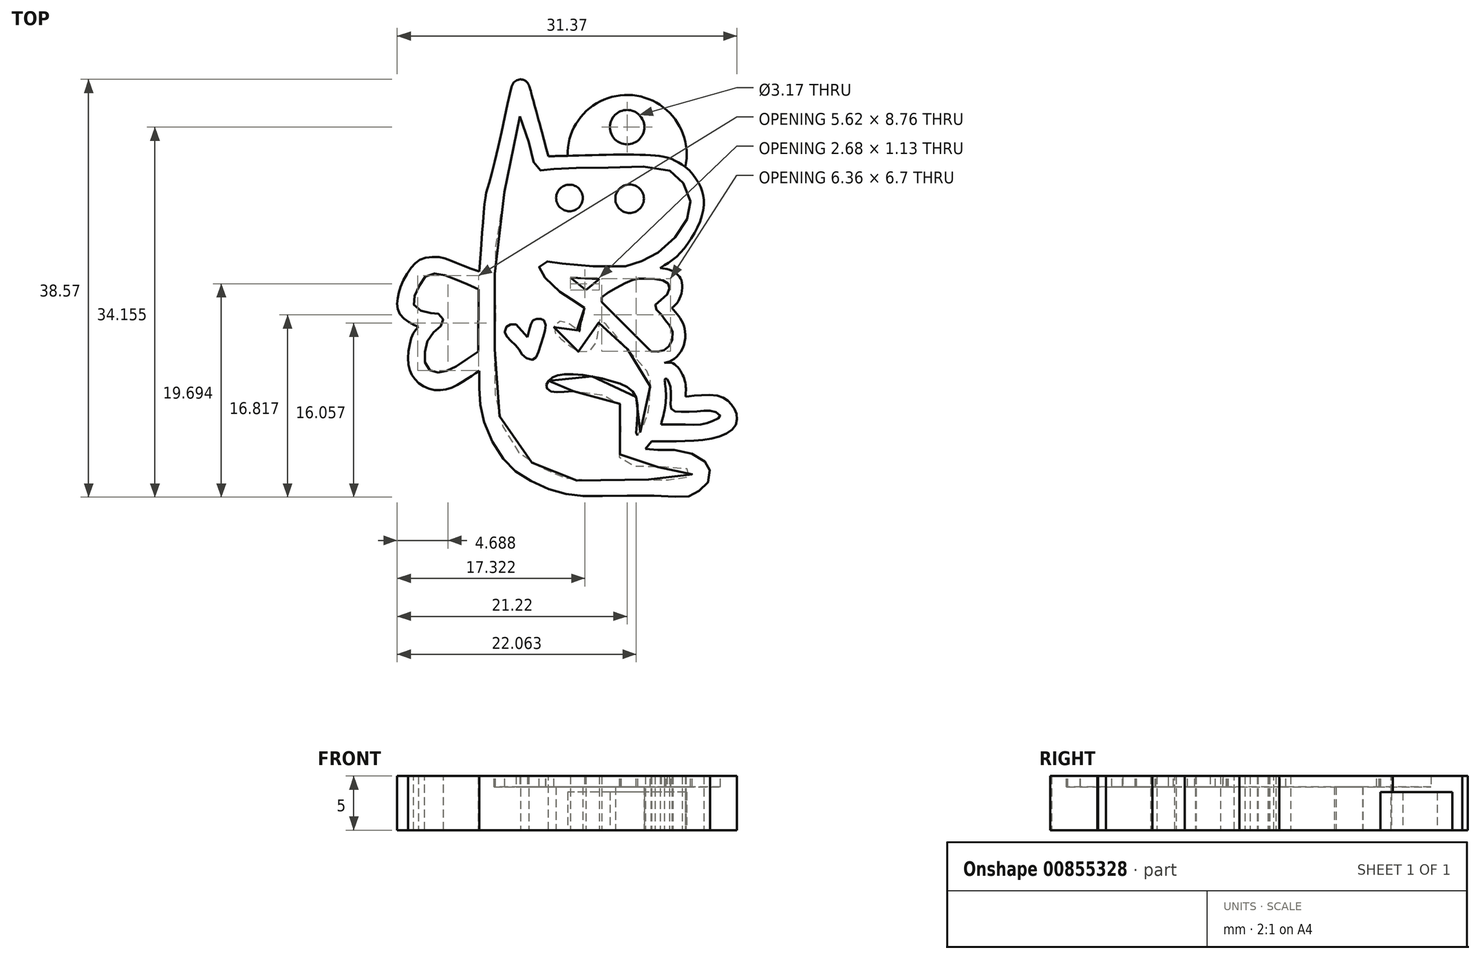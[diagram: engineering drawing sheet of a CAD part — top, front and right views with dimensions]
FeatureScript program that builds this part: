
annotation { "Feature Type Name" : "Feature", "Feature Type Description" : "" }
export const myFeature = defineFeature(function(context is Context, id is Id, definition is map)
    precondition{}
    {
        {
            var Q0;
            Q0=qCreatedBy(makeId("Top.planeOp"),FACE);
            var sketch = newSketch(context, id + "F0", { "sketchPlane" : qUnion([Q0])});
            skFitSpline(sketch, "E0", {"points": [v(-7.48, 15.74) * mm, v(-8.03, 15.56) * mm, v(-8.57, 13.92) * mm, v(-10.3, 6.44) * mm, v(-10.66, 5.2) * mm, v(-10.89, 3.24) * mm, v(-11.2, -1.02) * mm, v(-11.27, -2) * mm], "startDerivative": vector(-8.23, -1.23) * mm, "endDerivative": vector(-0.55, -7.97) * mm});
            skFitSpline(sketch, "E1", {"points": [v(-11.27, -2) * mm, v(-13.6, -1.14) * mm, v(-14.83, -0.68) * mm, v(-16.51, -0.82) * mm, v(-17.49, -1.57) * mm, v(-18.53, -3.31) * mm, v(-18.83, -4.6) * mm, v(-18.76, -5.67) * mm, v(-17.85, -6.63) * mm, v(-16.92, -7.1) * mm], "startDerivative": vector(-17.8, 6.14) * mm, "endDerivative": vector(9.73, -4.22) * mm});
            skFitSpline(sketch, "E2", {"points": [v(-16.92, -7.1) * mm, v(-17.49, -7.96) * mm, v(-17.85, -10.32) * mm, v(-17.3, -11.86) * mm, v(-15.85, -12.84) * mm, v(-14.06, -12.82) * mm, v(-12.36, -11.89) * mm, v(-11.27, -11.18) * mm], "startDerivative": vector(-5.4, -6.2) * mm, "endDerivative": vector(8.14, 5.18) * mm});
            skFitSpline(sketch, "E3", {"points": [v(-11.27, -11.18) * mm, v(-11.27, -13.54) * mm, v(-10.82, -15.97) * mm, v(-9.19, -19.15) * mm, v(-7.44, -20.82) * mm, v(-4.72, -22.14) * mm, v(-2.27, -22.7) * mm, v(0.89, -22.7) * mm, v(6.17, -22.75) * mm, v(8, -22.77) * mm, v(8.96, -22.3) * mm, v(9.87, -21.4) * mm, v(9.98, -20.26) * mm, v(9.57, -19.58) * mm, v(7.76, -18.62) * mm, v(5.35, -18.47) * mm, v(4.06, -18.4) * mm], "startDerivative": vector(-0.97, -36.57) * mm, "endDerivative": vector(-24.45, 2.03) * mm});
            skFitSpline(sketch, "E4", {"points": [v(4.06, -18.4) * mm, v(4.63, -17.67) * mm], "startDerivative": vector(0.57, 0.73) * mm, "endDerivative": vector(0.57, 0.73) * mm});
            skFitSpline(sketch, "E5", {"points": [v(4.63, -17.67) * mm, v(7.4, -17.67) * mm, v(10.52, -17.35) * mm, v(12.3, -16.33) * mm, v(12.45, -15.15) * mm, v(11.89, -14.16) * mm, v(10.77, -13.48) * mm, v(8.46, -13.48) * mm, v(7.76, -13.54) * mm], "startDerivative": vector(17.04, -0.15) * mm, "endDerivative": vector(-7.1, -0.7) * mm});
            skFitSpline(sketch, "E6", {"points": [v(7.76, -13.54) * mm, v(7.76, -12.48) * mm, v(7.42, -11.41) * mm, v(6.6, -10.48) * mm, v(5.78, -10.44) * mm], "startDerivative": vector(0.25, 4.28) * mm, "endDerivative": vector(-3.79, -0.53) * mm});
            skFitSpline(sketch, "E7", {"points": [v(5.78, -10.44) * mm, v(6.77, -10.03) * mm, v(7.64, -8.63) * mm, v(7.62, -7.1) * mm, v(7.13, -6.15) * mm, v(6.5, -5.37) * mm], "startDerivative": vector(5.5, 1.36) * mm, "endDerivative": vector(-3.67, 4.26) * mm});
            skFitSpline(sketch, "E8", {"points": [v(6.5, -5.37) * mm, v(7.15, -4.63) * mm, v(7.45, -3.35) * mm, v(7.2, -2.46) * mm, v(6.37, -1.89) * mm, v(5.41, -1.67) * mm], "startDerivative": vector(3.67, 3.27) * mm, "endDerivative": vector(-4.99, 0.71) * mm});
            skFitSpline(sketch, "E9", {"points": [v(5.41, -1.67) * mm, v(6.75, -0.77) * mm, v(8.14, 0.84) * mm, v(9.27, 3.14) * mm, v(9.4, 4.89) * mm, v(9, 6.06) * mm, v(7.95, 7.48) * mm, v(6.5, 8.37) * mm, v(5.41, 8.65) * mm, v(2.36, 8.8) * mm, v(-2.68, 8.7) * mm, v(-4.9, 8.64) * mm], "startDerivative": vector(17.1, 10.03) * mm, "endDerivative": vector(-20.94, -0.48) * mm});
            skFitSpline(sketch, "E10", {"points": [v(-4.9, 8.64) * mm, v(-6.63, 14.99) * mm, v(-6.71, 15.22) * mm], "startDerivative": vector(-2.7, 10.15) * mm, "endDerivative": vector(-0.37, 0.92) * mm});
            skFitSpline(sketch, "E11", {"points": [v(-6.71, 15.22) * mm, v(-6.9, 15.5) * mm, v(-7.21, 15.7) * mm, v(-7.48, 15.74) * mm], "startDerivative": vector(-0.44, 0.89) * mm, "endDerivative": vector(-0.86, 0.07) * mm});
            skFitSpline(sketch, "E12", {"points": [v(-11.36, -3.64) * mm, v(-12.73, -3.02) * mm, v(-14.07, -2.49) * mm, v(-15.1, -2.2) * mm, v(-16.11, -2.34) * mm, v(-16.74, -3.17) * mm, v(-17.27, -4.33) * mm, v(-17.3, -5.09) * mm, v(-16.72, -5.6) * mm, v(-15.75, -5.84) * mm, v(-15.14, -5.88) * mm, v(-14.73, -6.22) * mm, v(-14.6, -6.6) * mm, v(-14.98, -7.17) * mm, v(-15.66, -7.76) * mm, v(-16.2, -8.8) * mm, v(-16.33, -9.95) * mm, v(-16.13, -10.83) * mm, v(-15.5, -11.28) * mm, v(-14.81, -11.3) * mm, v(-14.02, -11.09) * mm, v(-12.85, -10.4) * mm, v(-11.39, -9.4) * mm], "startDerivative": vector(-23.85, 10.92) * mm, "endDerivative": vector(24.08, 16.28) * mm});
            skFitSpline(sketch, "E13", {"points": [v(-11.39, -9.4) * mm, v(-11.36, -3.64) * mm], "startDerivative": vector(0.02, 5.77) * mm, "endDerivative": vector(0.02, 5.77) * mm});
            skFitSpline(sketch, "E14", {"points": [v(0.02, -4.84) * mm, v(0.02, -4.37) * mm], "startDerivative": vector(0, 0.47) * mm, "endDerivative": vector(0, 0.47) * mm});
            skFitSpline(sketch, "E15", {"points": [v(0.02, -4.37) * mm, v(1, -3.7) * mm, v(2.53, -2.93) * mm, v(3.25, -2.69) * mm, v(4.18, -2.67) * mm, v(5.54, -2.79) * mm, v(6.13, -3.09) * mm, v(6.26, -3.5) * mm, v(5.96, -4.24) * mm, v(5.03, -4.98) * mm, v(4.98, -5.4) * mm, v(5.5, -5.94) * mm, v(6.02, -6.68) * mm, v(6.5, -7.36) * mm, v(6.52, -8.33) * mm, v(6.04, -9.12) * mm, v(5.38, -9.38) * mm, v(4.55, -9.36) * mm], "startDerivative": vector(12.8, 9.65) * mm, "endDerivative": vector(-14.93, 1.2) * mm});
            skFitSpline(sketch, "E16", {"points": [v(4.55, -9.36) * mm, v(0.02, -4.84) * mm], "startDerivative": vector(-4.52, 4.52) * mm, "endDerivative": vector(-4.52, 4.52) * mm});
            skFitSpline(sketch, "E17", {"points": [v(-2.88, -2.57) * mm, v(-1.45, -3.7) * mm], "startDerivative": vector(1.43, -1.13) * mm, "endDerivative": vector(1.43, -1.13) * mm});
            skFitSpline(sketch, "E18", {"points": [v(-1.45, -3.7) * mm, v(-0.2, -2.7) * mm], "startDerivative": vector(1.25, 1) * mm, "endDerivative": vector(1.25, 1) * mm});
            skFitSpline(sketch, "E19", {"points": [v(-0.2, -2.7) * mm, v(-2.88, -2.57) * mm], "startDerivative": vector(-2.68, 0.14) * mm, "endDerivative": vector(-2.68, 0.14) * mm});
            skCircle(sketch, "E20", {"center": v(-2.96, 4.79) * mm, "radius": 1.23 * mm});
            skCircle(sketch, "E21", {"center": v(2.6, 4.72) * mm, "radius": 1.32 * mm});
            skFitSpline(sketch, "E22", {"points": [v(-7.53, 12.33) * mm, v(-8.43, 7.98) * mm, v(-9.84, -0.28) * mm, v(-9.8, -3.59) * mm, v(-9.88, -9.71) * mm, v(-9.75, -13.89) * mm, v(-8.61, -17.38) * mm, v(-6.75, -19.47) * mm, v(-4.53, -20.55) * mm, v(-2.76, -21.23) * mm, v(1.1, -21.23) * mm, v(6.04, -21.23) * mm, v(7.76, -21.1) * mm, v(8.35, -20.74) * mm, v(8.22, -20.5) * mm, v(7.72, -20.15) * mm, v(6.08, -20.06) * mm, v(2.82, -19.96) * mm, v(1.73, -19.51) * mm, v(1.82, -17.97) * mm, v(1.68, -14.8) * mm, v(1.64, -14.11) * mm, v(-0.04, -13.39) * mm, v(-3.03, -13.07) * mm, v(-4.67, -13.07) * mm, v(-5.12, -12.57) * mm, v(-4.8, -12.03) * mm, v(-4.03, -11.57) * mm, v(-1.63, -11.57) * mm, v(1.37, -12.25) * mm, v(3, -13.2) * mm, v(3.32, -15.38) * mm, v(3.27, -17.15) * mm, v(4.13, -15.6) * mm, v(4.45, -13.66) * mm, v(4.5, -12.2) * mm, v(4.31, -11.4) * mm, v(2.5, -9.3) * mm, v(0.55, -7.04) * mm, v(-0.18, -6.45) * mm, v(-0.31, -7.67) * mm, v(-1.08, -9.35) * mm, v(-2.26, -9.35) * mm, v(-3.44, -8.49) * mm, v(-4.21, -7.76) * mm, v(-4.35, -7) * mm, v(-3.85, -6.58) * mm, v(-2.94, -6.8) * mm, v(-2.35, -7.3) * mm, v(-2.08, -7.58) * mm, v(-2, -7.04) * mm, v(-1.8, -6.31) * mm, v(-1.58, -5.36) * mm], "startDerivative": vector(-26.35, -124.87) * mm, "endDerivative": vector(15.4, 70.83) * mm});
            skFitSpline(sketch, "E23", {"points": [v(-1.58, -5.36) * mm, v(-2.73, -4.58) * mm, v(-3.6, -4.07) * mm, v(-5.23, -2.57) * mm, v(-5.77, -1.75) * mm, v(-5.5, -1.21) * mm, v(-4.9, -1.08) * mm, v(-3.32, -1.3) * mm, v(2.46, -1.5) * mm, v(3.8, -0.99) * mm, v(5.8, 0.14) * mm, v(7.66, 2.41) * mm, v(8.22, 4.34) * mm, v(7.43, 6.3) * mm, v(5.77, 7.49) * mm, v(-0.37, 7.56) * mm, v(-4.28, 7.49) * mm, v(-5.42, 7.32) * mm, v(-6.05, 7.53) * mm, v(-6.4, 8.75) * mm, v(-7.53, 12.33) * mm], "startDerivative": vector(-28.76, 20.87) * mm, "endDerivative": vector(-20.2, 56.95) * mm});
            skFitSpline(sketch, "E24", {"points": [v(6.05, -11.93) * mm, v(5.88, -11.91) * mm, v(5.92, -12.81) * mm, v(5.88, -14.4) * mm, v(5.5, -16.13) * mm], "startDerivative": vector(-1.93, 0.79) * mm, "endDerivative": vector(-1.34, -5.2) * mm});
            skFitSpline(sketch, "E25", {"points": [v(5.5, -16.13) * mm, v(7.42, -16.13) * mm, v(9.23, -16.13) * mm, v(10.3, -15.79) * mm, v(10.97, -15.37) * mm, v(10.32, -14.9) * mm, v(9.25, -14.89) * mm, v(7.46, -14.97) * mm, v(6.5, -14.77) * mm, v(6.37, -14.2) * mm, v(6.41, -13.25) * mm, v(6.26, -12.31) * mm, v(6.05, -11.93) * mm], "startDerivative": vector(16.85, 0.3) * mm, "endDerivative": vector(-4.2, 6.12) * mm});
            skFitSpline(sketch, "E26", {"points": [v(-7.9, -6.9) * mm, v(-6.84, -8.05) * mm], "startDerivative": vector(1.06, -1.15) * mm, "endDerivative": vector(1.06, -1.15) * mm});
            skFitSpline(sketch, "E27", {"points": [v(-6.84, -8.05) * mm, v(-6.51, -6.9) * mm, v(-6.23, -6.42) * mm, v(-5.74, -6.38) * mm, v(-5.4, -6.45) * mm, v(-5.17, -7.03) * mm, v(-5.4, -8.05) * mm, v(-5.9, -9.66) * mm, v(-6.35, -10.14) * mm, v(-7.22, -9.78) * mm, v(-7.7, -9.05) * mm, v(-8.47, -8.3) * mm, v(-8.92, -7.64) * mm, v(-8.66, -7) * mm, v(-7.9, -6.9) * mm], "startDerivative": vector(3.69, 14.28) * mm, "endDerivative": vector(12.33, -0.92) * mm});
            skCircle(sketch, "E28", {"center": v(2.36, 11.32) * mm, "radius": 1.59 * mm});
            skArc(sketch, "E29.trimOffspring", {"start": v(7.74, 7.66) * mm, "mid": v(2.88, 14.27) * mm, "end": v(-3.14, 8.68) * mm});
            skSolve(sketch);
        }
        {
            var Q0;
            Q0=makeQuery(id+"F0.imprint","IMPRINT",FACE,{"disambiguationData":[TD([[makeQuery(id+"F0.imprint","IMPRINT",EDGE,{"derivedFrom":sQuery(id+"F0.wireOp",EDGE,"E28")}),-1.0]])]});
            extrude(context, id + "F1", {"entities" : qUnion([Q0]), "depth" : 3.5 * mm, "offsetDistance" : 25 * mm});
        }
        {
            var Q0;
            Q0=makeQuery(id+"F0.imprint","IMPRINT",FACE,{"disambiguationData":[TD([[makeQuery(id+"F0.imprint","IMPRINT",EDGE,{"derivedFrom":sQuery(id+"F0.wireOp",EDGE,"E0")}),1.0]])]});
            var Q1;
            Q1=makeQuery(id+"F0.imprint","IMPRINT",FACE,{"disambiguationData":[TD([[makeQuery(id+"F0.imprint","IMPRINT",EDGE,{"derivedFrom":sQuery(id+"F0.wireOp",EDGE,"E26")}),-1.0]])]});
            extrude(context, id + "F2", {"entities" : qUnion([Q0, Q1]), "operationType" : NewBodyOperationType.ADD, "depth" : 5 * mm, "offsetDistance" : 25 * mm});
        }
        {
            var Q0;
            Q0=makeQuery(id+"F0.imprint","IMPRINT",FACE,{"disambiguationData":[TD([[makeQuery(id+"F0.imprint","IMPRINT",EDGE,{"derivedFrom":sQuery(id+"F0.wireOp",EDGE,"E20")}),-1.0]])]});
            var Q1;
            Q1=makeQuery(id+"F0.imprint","IMPRINT",FACE,{"disambiguationData":[TD([[makeQuery(id+"F0.imprint","IMPRINT",EDGE,{"derivedFrom":sQuery(id+"F0.wireOp",EDGE,"E24")}),1.0]])]});
            extrude(context, id + "F3", {"entities" : qUnion([Q0, Q1]), "operationType" : NewBodyOperationType.ADD, "depth" : 4 * mm, "offsetDistance" : 25 * mm});
        }
    });
